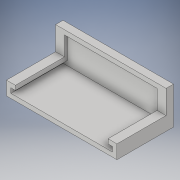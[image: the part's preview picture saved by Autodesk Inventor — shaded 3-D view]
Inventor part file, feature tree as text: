
AUTODESK INVENTOR PART (.ipt)
format: ipt  version: 2019 (Build 230136000, 136)  size: 139,776 bytes
history: native  units: mm
features: extrude x3, sketch x3, other x1
ambient origin geometry x8: Origin, YZ Plane, XZ Plane, XY Plane, X Axis, Y Axis, Z Axis, Center Point
bodies: Body1 (feature_tree), Body2 (feature_tree)
feature tree (7):
  other  "Твердое тело1"
  extrude  "Выдавливание1"  Depth=68.2mm
  extrude  "Выдавливание2"  Depth=3.0mm
  extrude  "Выдавливание3"  Depth=3.0mm
  sketch  "Эскиз1"
  sketch  "Эскиз2"
  sketch  "Эскиз3"
